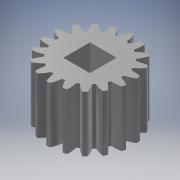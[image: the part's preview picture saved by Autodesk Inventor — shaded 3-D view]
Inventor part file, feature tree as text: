
AUTODESK INVENTOR PART (.ipt)
format: ipt  version: 2017 (Build 210142000, 142)  size: 217,600 bytes
history: native  units: mm (DEFAULTED — no unit token found)
features: plane x3, other x3, sketch x3, extrude x2
ambient origin geometry x8: Origin, YZ Plane, XZ Plane, XY Plane, X Axis, Y Axis, Z Axis, Center Point
bodies: Solid1 (feature_tree)
feature tree (11):
  extrude  "Extrusion1"  Depth=20.0mm TaperAngle=0.0deg
  plane  "Work Plane2"
  plane  "Work Plane8"
  plane  "Work Plane9"
  other  "Spur Gear"
  extrude  "Extrusion2"  Depth=10.0mm TaperAngle=0.0deg
  sketch  "Sketch1"  dims[d0=29.976768mm d1=20.0mm d2=0.0mm]
  sketch  "Sketch2"  dims[d3=27.169811mm d4=10.0mm d5=0.0mm]
  other  "Srf1"
  sketch  "Sketch3"  dims[d16=80.0mm d17=0.0mm d34=1.745329mm d39=0.0mm d41=0.0mm d43=80.0mm d46=80.0mm d47=0.0mm d48=0.0mm d49=9.525mm d50=10.0mm d51=0.0mm]
  other  "Pitch Diameter"
